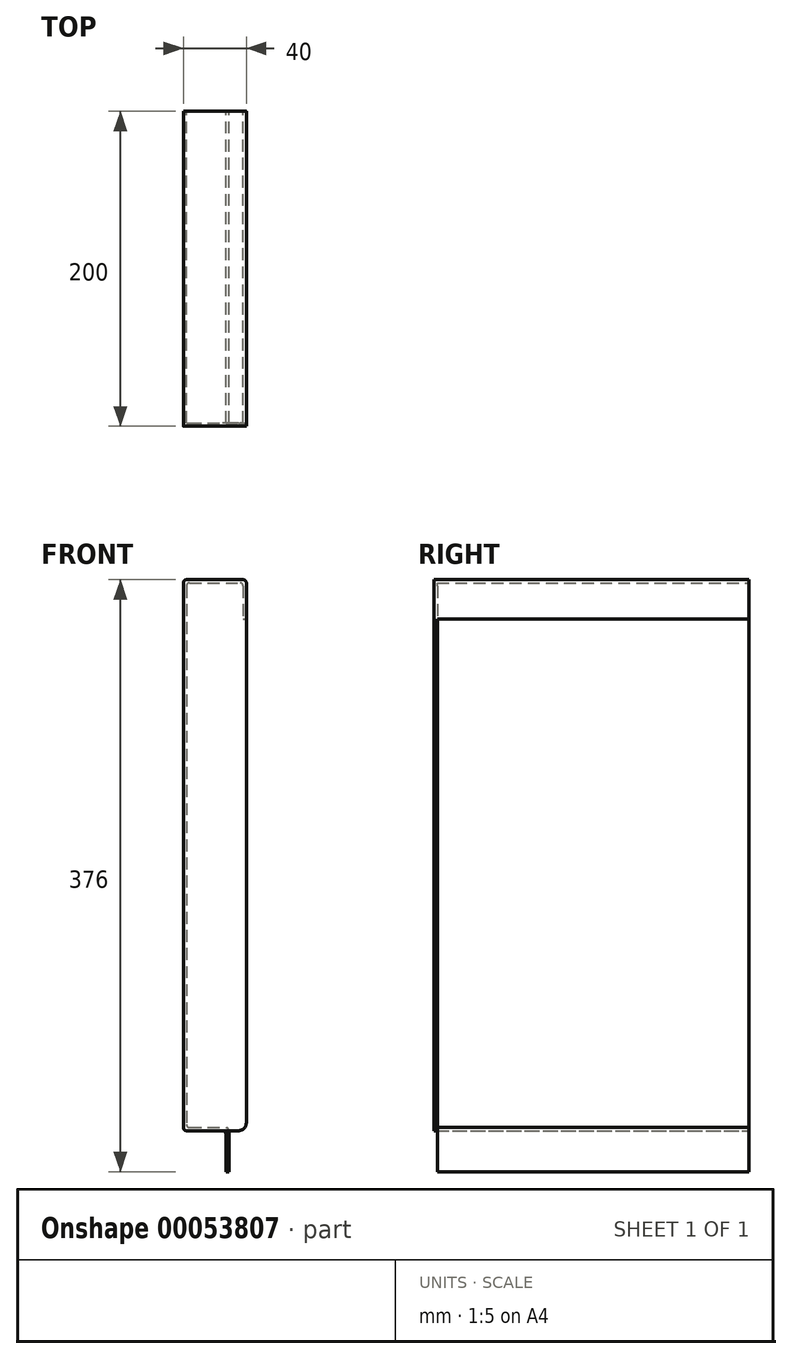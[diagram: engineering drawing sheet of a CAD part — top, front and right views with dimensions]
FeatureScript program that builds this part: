
annotation { "Feature Type Name" : "Feature", "Feature Type Description" : "" }
export const myFeature = defineFeature(function(context is Context, id is Id, definition is map)
    precondition{}
    {
        {
            var Q0;
            Q0=qCreatedBy(makeId("Front.planeOp"),FACE);
            var sketch = newSketch(context, id + "F0", { "sketchPlane" : qUnion([Q0])});
            skLineSegment(sketch, "E0", {"start": v(0, 0) * mm, "end": v(0, -350) * mm});
            skLineSegment(sketch, "E1", {"start": v(0, -350) * mm, "end": v(27, -350) * mm});
            skLineSegment(sketch, "E2", {"start": v(27, -350) * mm, "end": v(27, -376) * mm});
            skLineSegment(sketch, "E3", {"start": v(0, 0) * mm, "end": v(40, 0) * mm});
            skLineSegment(sketch, "E4", {"start": v(40, 0) * mm, "end": v(40, -25) * mm});
            skLineSegment(sketch, "E5.0", {"start": v(38, -2) * mm, "end": v(38, -25) * mm});
            skLineSegment(sketch, "E5.1", {"start": v(29, -348) * mm, "end": v(29, -376) * mm});
            skLineSegment(sketch, "E5.2", {"start": v(2, -348) * mm, "end": v(29, -348) * mm});
            skLineSegment(sketch, "E5.3", {"start": v(2, -2) * mm, "end": v(2, -348) * mm});
            skLineSegment(sketch, "E5.4", {"start": v(2, -2) * mm, "end": v(38, -2) * mm});
            skLineSegment(sketch, "E6", {"start": v(38, -25) * mm, "end": v(40, -25) * mm});
            skLineSegment(sketch, "E7", {"start": v(27, -376) * mm, "end": v(29, -376) * mm});
            skSolve(sketch);
        }
        {
            var Q0;
            Q0=qCreatedBy(makeId("Top.planeOp"),FACE);
            var sketch = newSketch(context, id + "F1", { "sketchPlane" : qUnion([Q0])});
            skLineSegment(sketch, "E8", {"start": v(0, 0) * mm, "end": v(0, 198) * mm});
            skSolve(sketch);
        }
        {
            var Q0;
            Q0 = qSketchRegion(id + "F0", true);
            var Q1;
            Q1 = qConstructionFilter(qBodyType(qCreatedBy(id + "F1" ,EDGE), BodyType.WIRE), ConstructionObject.NO);
            sweep(context, id + "F2", {"profiles" : qUnion([Q0]), "path" : qUnion([Q1])});
        }
        {
            var Q0;
            Q0=makeQuery(id+"F2.opSweep","CAP_FACE",FACE,{"disambiguationData":[OSD([sQuery(id+"F0.wireOp",EDGE,"E0"),sQuery(id+"F0.wireOp",EDGE,"E1"),sQuery(id+"F0.wireOp",EDGE,"E2"),sQuery(id+"F0.wireOp",EDGE,"E3"),sQuery(id+"F0.wireOp",EDGE,"E4"),sQuery(id+"F0.wireOp",EDGE,"E5.0"),sQuery(id+"F0.wireOp",EDGE,"E5.1"),sQuery(id+"F0.wireOp",EDGE,"E5.2"),sQuery(id+"F0.wireOp",EDGE,"E5.3"),sQuery(id+"F0.wireOp",EDGE,"E5.4"),sQuery(id+"F0.wireOp",EDGE,"E6"),sQuery(id+"F0.wireOp",EDGE,"E7"),sQuery(id+"F1.wireOp",VERTEX,"E8.start")])],"isStart":true});
            var sketch = newSketch(context, id + "F3", { "sketchPlane" : qUnion([Q0])});
            skLineSegment(sketch, "E9.0", {"start": v(40, 0) * mm, "end": v(0, 0) * mm});
            skLineSegment(sketch, "E10.0", {"start": v(0, -350) * mm, "end": v(0, 0) * mm});
            skPoint(sketch, "E11.0.end.orphan", {"position": v(27, -350) * mm});
            skPoint(sketch, "E12.0.start.orphan", {"position": v(40, -25) * mm});
            skLineSegment(sketch, "E13", {"start": v(40, 0) * mm, "end": v(40, -345) * mm});
            skLineSegment(sketch, "E14", {"start": v(35, -350) * mm, "end": v(0, -350) * mm});
            skPoint(sketch, "E15.visualSharp", {"position": v(40, -350) * mm});
            skArc(sketch, "E15.filletArc", {"start": v(35, -350) * mm, "mid": v(38.54, -348.54) * mm, "end": v(40, -345) * mm});
            skSolve(sketch);
        }
        {
            var Q0;
            Q0 = qSketchRegion(id + "F3", true);
            extrude(context, id + "F4", {"entities" : qUnion([Q0]), "depth" : 2 * mm});
        }
        {
            var Q0;
            Q0=makeQuery(id+"F2.opSweep","SWEPT_BODY",BODY,{"disambiguationData":[OSD([sQuery(id+"F0.wireOp",EDGE,"E0"),sQuery(id+"F0.wireOp",EDGE,"E1"),sQuery(id+"F0.wireOp",EDGE,"E2"),sQuery(id+"F0.wireOp",EDGE,"E3"),sQuery(id+"F0.wireOp",EDGE,"E4"),sQuery(id+"F0.wireOp",EDGE,"E5.0"),sQuery(id+"F0.wireOp",EDGE,"E5.1"),sQuery(id+"F0.wireOp",EDGE,"E5.2"),sQuery(id+"F0.wireOp",EDGE,"E5.3"),sQuery(id+"F0.wireOp",EDGE,"E5.4"),sQuery(id+"F0.wireOp",EDGE,"E6"),sQuery(id+"F0.wireOp",EDGE,"E7"),sQuery(id+"F1.wireOp",EDGE,"E8")])]});
            var Q1;
            Q1=makeQuery(id+"F4.opExtrude","SWEPT_BODY",BODY,{"disambiguationData":[OSD([sQuery(id+"F3.wireOp",EDGE,"E9.0"),sQuery(id+"F3.wireOp",EDGE,"E10.0"),sQuery(id+"F3.wireOp",EDGE,"E13"),sQuery(id+"F3.wireOp",EDGE,"E14"),sQuery(id+"F3.wireOp",EDGE,"E15.filletArc")])]});
            booleanBodies(context, id + "F5", {"operationType" : BooleanOperationType.UNION, "tools" : qUnion([Q0, Q1])});
        }
        {
            var Q0;
            Q0=makeQuery(id+"F5.opBoolean","MERGE",EDGE,{"derivedFrom":[makeQuery(id+"F2.opSweep","SWEPT_EDGE",EDGE,{"disambiguationData":[OSD([sQuery(id+"F0.wireOp",EDGE,"E3"),sQuery(id+"F0.wireOp",EDGE,"E4"),sQuery(id+"F1.wireOp",EDGE,"E8")])]}),makeQuery(id+"F4.opExtrude","SWEPT_EDGE",EDGE,{"disambiguationData":[OSD([sQuery(id+"F3.wireOp",EDGE,"E9.0"),sQuery(id+"F3.wireOp",EDGE,"E13")])]})]});
            var Q1;
            Q1=makeQuery(id+"F5.opBoolean","MERGE",EDGE,{"derivedFrom":[makeQuery(id+"F2.opSweep","SWEPT_EDGE",EDGE,{"disambiguationData":[OSD([sQuery(id+"F0.wireOp",EDGE,"E0"),sQuery(id+"F0.wireOp",EDGE,"E3"),sQuery(id+"F1.wireOp",EDGE,"E8")])]}),makeQuery(id+"F4.opExtrude","SWEPT_EDGE",EDGE,{"disambiguationData":[OSD([sQuery(id+"F3.wireOp",EDGE,"E9.0"),sQuery(id+"F3.wireOp",EDGE,"E10.0")])]})]});
            var Q2;
            Q2=makeQuery(id+"F2.opSweep","SWEPT_EDGE",EDGE,{"disambiguationData":[OSD([sQuery(id+"F0.wireOp",EDGE,"E5.1"),sQuery(id+"F0.wireOp",EDGE,"E5.2"),sQuery(id+"F1.wireOp",EDGE,"E8")])]});
            var Q3;
            Q3=makeQuery(id+"F2.opSweep","SWEPT_EDGE",EDGE,{"disambiguationData":[OSD([sQuery(id+"F0.wireOp",EDGE,"E5.2"),sQuery(id+"F0.wireOp",EDGE,"E5.3"),sQuery(id+"F1.wireOp",EDGE,"E8")])]});
            var Q4;
            Q4=makeQuery(id+"F2.opSweep","SWEPT_EDGE",EDGE,{"disambiguationData":[OSD([sQuery(id+"F0.wireOp",EDGE,"E1"),sQuery(id+"F0.wireOp",EDGE,"E2"),sQuery(id+"F1.wireOp",EDGE,"E8")])]});
            var Q5;
            Q5=makeQuery(id+"F5.opBoolean","MERGE",EDGE,{"derivedFrom":[makeQuery(id+"F2.opSweep","SWEPT_EDGE",EDGE,{"disambiguationData":[OSD([sQuery(id+"F0.wireOp",EDGE,"E0"),sQuery(id+"F0.wireOp",EDGE,"E1"),sQuery(id+"F1.wireOp",EDGE,"E8")])]}),makeQuery(id+"F4.opExtrude","SWEPT_EDGE",EDGE,{"disambiguationData":[OSD([sQuery(id+"F3.wireOp",EDGE,"E10.0"),sQuery(id+"F3.wireOp",EDGE,"E14")])]})]});
            var Q6;
            Q6=makeQuery(id+"F2.opSweep","SWEPT_EDGE",EDGE,{"disambiguationData":[OSD([sQuery(id+"F0.wireOp",EDGE,"E5.3"),sQuery(id+"F0.wireOp",EDGE,"E5.4"),sQuery(id+"F1.wireOp",EDGE,"E8")])]});
            var Q7;
            Q7=makeQuery(id+"F2.opSweep","SWEPT_EDGE",EDGE,{"disambiguationData":[OSD([sQuery(id+"F0.wireOp",EDGE,"E5.0"),sQuery(id+"F0.wireOp",EDGE,"E5.4"),sQuery(id+"F1.wireOp",EDGE,"E8")])]});
            fillet(context, id + "F6", {"entities" : qUnion([Q0, Q1, Q2, Q3, Q4, Q5, Q6, Q7]), "radius" : 2 * mm, "tangentPropagation" : true, "allowEdgeOverflow" : false});
        }
    });
